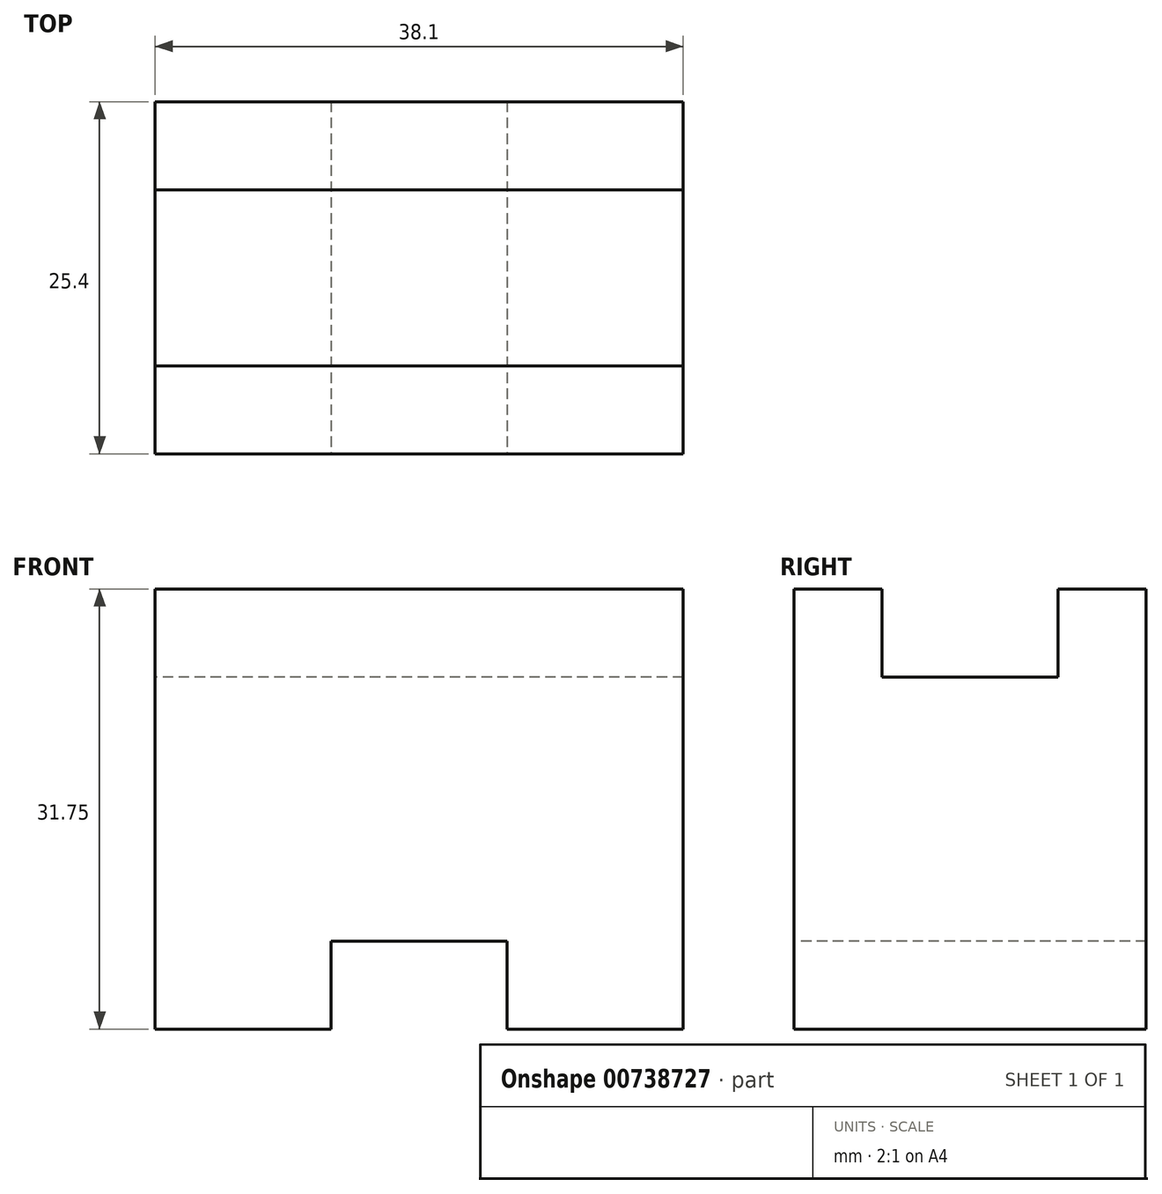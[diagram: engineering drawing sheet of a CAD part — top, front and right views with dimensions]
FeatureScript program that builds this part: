
annotation { "Feature Type Name" : "Feature", "Feature Type Description" : "" }
export const myFeature = defineFeature(function(context is Context, id is Id, definition is map)
    precondition{}
    {
        {
            var Q0;
            Q0=qCreatedBy(makeId("Right.planeOp"),FACE);
            var sketch = newSketch(context, id + "F0", { "sketchPlane" : qUnion([Q0])});
            skLineSegment(sketch, "E0", {"start": v(0, 0) * mm, "end": v(25.4, 0) * mm});
            skLineSegment(sketch, "E1", {"start": v(25.4, 0) * mm, "end": v(25.4, 31.75) * mm});
            skLineSegment(sketch, "E2", {"start": v(25.4, 31.75) * mm, "end": v(19.05, 31.75) * mm});
            skLineSegment(sketch, "E3", {"start": v(19.05, 31.75) * mm, "end": v(19.05, 25.4) * mm});
            skLineSegment(sketch, "E4", {"start": v(19.05, 25.4) * mm, "end": v(6.35, 25.4) * mm});
            skLineSegment(sketch, "E5", {"start": v(6.35, 25.4) * mm, "end": v(6.35, 31.75) * mm});
            skLineSegment(sketch, "E6", {"start": v(6.35, 31.75) * mm, "end": v(0, 31.75) * mm});
            skLineSegment(sketch, "E7", {"start": v(0, 31.75) * mm, "end": v(0, 0) * mm});
            skSolve(sketch);
        }
        {
            var Q0;
            Q0=makeQuery(id+"F0.imprint","IMPRINT",FACE,{"disambiguationData":[TD([[makeQuery(id+"F0.imprint","IMPRINT",EDGE,{"derivedFrom":sQuery(id+"F0.wireOp",EDGE,"E0")}),1.0]])]});
            extrude(context, id + "F1", {"entities" : qUnion([Q0]), "depth" : 38.1 * mm, "offsetDistance" : 25.4 * mm});
        }
        {
            var Q0;
            Q0=qCreatedBy(makeId("Front.planeOp"),FACE);
            var sketch = newSketch(context, id + "F2", { "sketchPlane" : qUnion([Q0])});
            skLineSegment(sketch, "E8", {"start": v(12.7, 0) * mm, "end": v(12.7, 6.35) * mm});
            skLineSegment(sketch, "E9", {"start": v(12.7, 6.35) * mm, "end": v(25.4, 6.35) * mm});
            skLineSegment(sketch, "E10", {"start": v(25.4, 6.35) * mm, "end": v(25.4, 0) * mm});
            skLineSegment(sketch, "E11", {"start": v(25.4, 0) * mm, "end": v(12.7, 0) * mm});
            skLineSegment(sketch, "E12", {"start": v(0, 0) * mm, "end": v(12.7, 0) * mm});
            skSolve(sketch);
        }
        {
            var Q0;
            Q0=makeQuery(id+"F2.imprint","IMPRINT",FACE,{"disambiguationData":[TD([[makeQuery(id+"F2.imprint","IMPRINT",EDGE,{"derivedFrom":sQuery(id+"F2.wireOp",EDGE,"E8")}),-1.0]])]});
            extrude(context, id + "F3", {"entities" : qUnion([Q0]), "operationType" : NewBodyOperationType.REMOVE, "oppositeDirection" : true, "depth" : 25.4 * mm, "offsetDistance" : 25.4 * mm});
        }
    });
